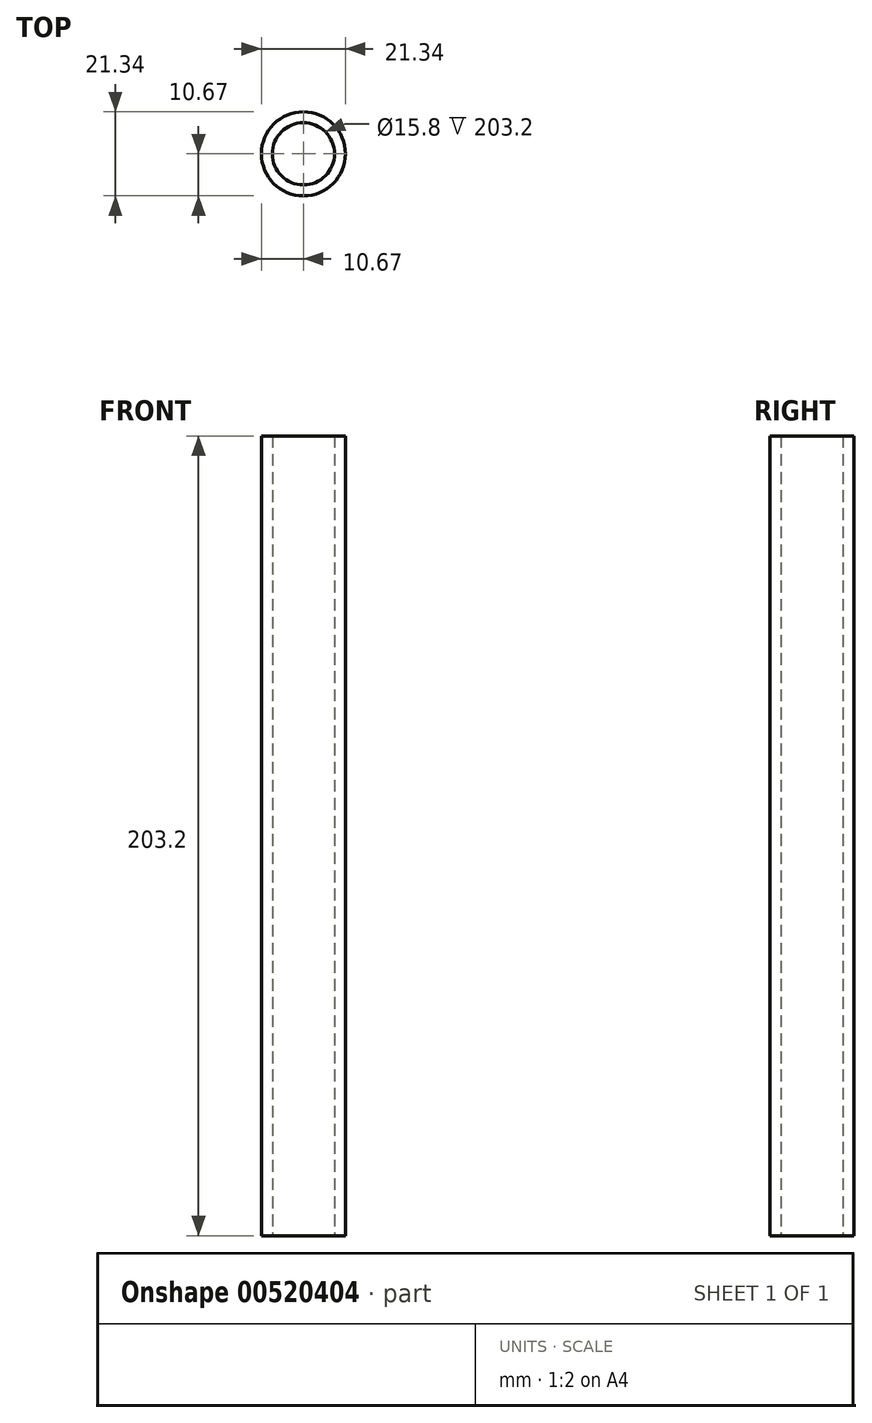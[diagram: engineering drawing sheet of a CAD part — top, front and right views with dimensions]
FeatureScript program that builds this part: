
annotation { "Feature Type Name" : "Feature", "Feature Type Description" : "" }
export const myFeature = defineFeature(function(context is Context, id is Id, definition is map)
    precondition{}
    {
        {
            var Q0;
            Q0=qCreatedBy(makeId("Top.planeOp"),FACE);
            var sketch = newSketch(context, id + "F0", { "sketchPlane" : qUnion([Q0])});
            skCircle(sketch, "E0", {"center": v(0, 0) * mm, "radius": 7.9 * mm});
            skCircle(sketch, "E1", {"center": v(0, 0) * mm, "radius": 10.67 * mm});
            skSolve(sketch);
        }
        {
            var Q0;
            Q0=makeQuery(id+"F0.imprint","IMPRINT",FACE,{"disambiguationData":[TD([[makeQuery(id+"F0.imprint","IMPRINT",EDGE,{"derivedFrom":sQuery(id+"F0.wireOp",EDGE,"E0")}),-1.0]])]});
            extrude(context, id + "F1", {"entities" : qUnion([Q0]), "depth" : 127 * mm, "offsetDistance" : 25.4 * mm});
        }
        {
            var Q0;
            Q0=makeQuery(id+"F1.opExtrude","CAP_FACE",FACE,{"disambiguationData":[OSD([sQuery(id+"F0.wireOp",EDGE,"E0"),sQuery(id+"F0.wireOp",EDGE,"E1")])],"isStart":false});
            extrude(context, id + "F2", {"entities" : qUnion([Q0]), "operationType" : NewBodyOperationType.ADD, "depth" : 76.2 * mm, "offsetDistance" : 25.4 * mm});
        }
    });
